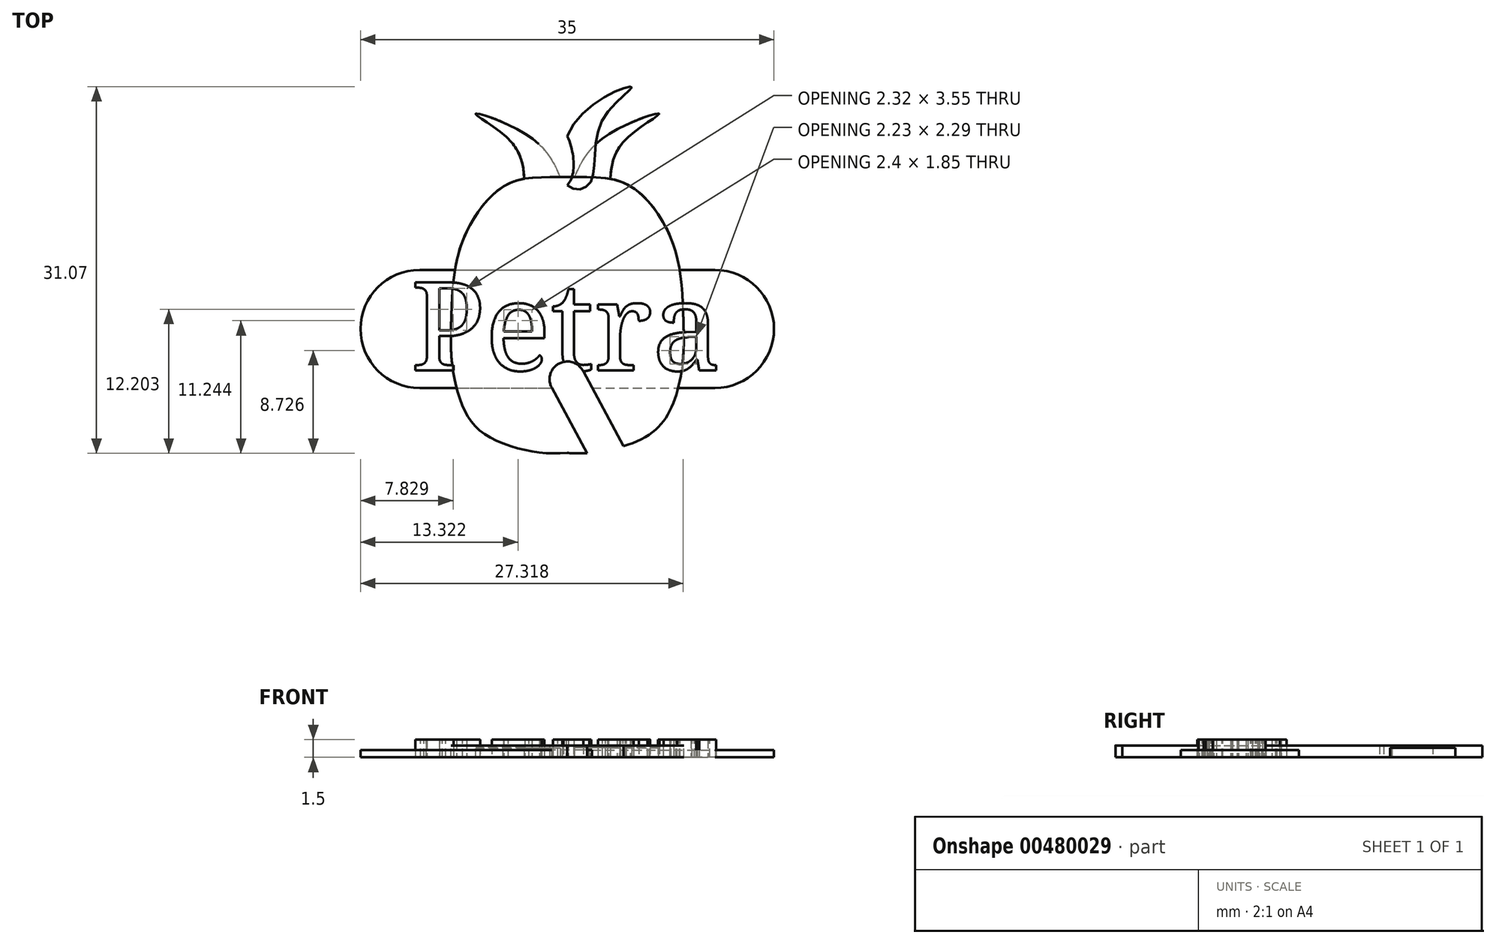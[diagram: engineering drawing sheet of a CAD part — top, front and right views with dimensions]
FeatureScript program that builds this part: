
annotation { "Feature Type Name" : "Feature", "Feature Type Description" : "" }
export const myFeature = defineFeature(function(context is Context, id is Id, definition is map)
    precondition{}
    {
        {
            var Q0;
            Q0=qCreatedBy(makeId("Top.planeOp"),FACE);
            var sketch = newSketch(context, id + "F0", { "sketchPlane" : qUnion([Q0])});
            skText(sketch, "E0", { "text": "Petra", "fontName": "NotoSerif-Regular.ttf"});
            const initialGuessF0  = {"E0": [-0.01327, -0.0075, 1, 0, 0.0075]};
            skSetInitialGuess(sketch, initialGuessF0);
            skSolve(sketch);
        }
        {
            var Q0;
            Q0 = qSketchRegion(id + "F0", true);
            extrude(context, id + "F1", {"entities" : qUnion([Q0]), "depth" : 1.5 * mm, "offsetDistance" : 25 * mm});
        }
        {
            var Q0;
            Q0=qCreatedBy(makeId("Top.planeOp"),FACE);
            var sketch = newSketch(context, id + "F2", { "sketchPlane" : qUnion([Q0])});
            skFitSpline(sketch, "E1", {"points": [v(0, -14.5) * mm, v(-3.65, -14.24) * mm, v(-7.11, -12.83) * mm, v(-8.78, -10.71) * mm, v(-9.74, -7.05) * mm, v(-9.8, -2.69) * mm, v(-9.49, 1.16) * mm, v(-8.52, 4.24) * mm, v(-6.73, 6.94) * mm, v(-4.16, 8.6) * mm, v(0, 8.86) * mm], "startDerivative": vector(-36.01, -3.1) * mm, "endDerivative": vector(39.07, 0.66) * mm});
            skFitSpline(sketch, "E2.MirrorCS", {"points": [v(0, -14.5) * mm, v(3.65, -14.24) * mm, v(7.11, -12.83) * mm, v(8.78, -10.71) * mm, v(9.74, -7.05) * mm, v(9.8, -2.69) * mm, v(9.49, 1.16) * mm, v(8.52, 4.24) * mm, v(6.73, 6.94) * mm, v(4.16, 8.6) * mm, v(0, 8.86) * mm], "startDerivative": vector(36.01, -3.1) * mm, "endDerivative": vector(-39.07, 0.66) * mm});
            skSolve(sketch);
        }
        {
            var Q0;
            Q0=makeQuery(id+"F2.imprint","IMPRINT",FACE,{"disambiguationData":[TD([[makeQuery(id+"F2.imprint","IMPRINT",EDGE,{"derivedFrom":sQuery(id+"F2.wireOp",EDGE,"E1")}),-1.0]])]});
            extrude(context, id + "F3", {"entities" : qUnion([Q0]), "depth" : 1 * mm, "offsetDistance" : 25 * mm});
        }
        {
            var Q0;
            Q0=qCreatedBy(makeId("Top.planeOp"),FACE);
            var sketch = newSketch(context, id + "F4", { "sketchPlane" : qUnion([Q0])});
            skFitSpline(sketch, "E3", {"points": [v(-3.62, 8.13) * mm, v(-4.76, 11.85) * mm, v(-7.76, 14.23) * mm, v(-3.16, 12.26) * mm, v(-0.47, 8.54) * mm], "startDerivative": vector(-0.55, 16.12) * mm, "endDerivative": vector(6.29, -15.12) * mm});
            skLineSegment(sketch, "E4", {"start": v(-3.62, 8.13) * mm, "end": v(-0.47, 8.54) * mm});
            skFitSpline(sketch, "E5.MirrorCS", {"points": [v(3.62, 8.13) * mm, v(4.76, 11.85) * mm, v(7.76, 14.23) * mm, v(3.16, 12.26) * mm, v(0.47, 8.54) * mm], "startDerivative": vector(0.55, 16.12) * mm, "endDerivative": vector(-6.29, -15.12) * mm});
            skLineSegment(sketch, "E6", {"start": v(0.47, 8.54) * mm, "end": v(3.62, 8.13) * mm});
            skSolve(sketch);
        }
        {
            var Q0;
            Q0=makeQuery(id+"F4.imprint","IMPRINT",FACE,{"disambiguationData":[TD([[makeQuery(id+"F4.imprint","IMPRINT",EDGE,{"derivedFrom":sQuery(id+"F4.wireOp",EDGE,"E3")}),-1.0]])]});
            var Q1;
            Q1=makeQuery(id+"F4.imprint","IMPRINT",FACE,{"disambiguationData":[TD([[makeQuery(id+"F4.imprint","IMPRINT",EDGE,{"derivedFrom":sQuery(id+"F4.wireOp",EDGE,"E5.MirrorCS")}),1.0]])]});
            extrude(context, id + "F5", {"entities" : qUnion([Q0, Q1]), "operationType" : NewBodyOperationType.ADD, "depth" : 0.8 * mm, "offsetDistance" : 25 * mm});
        }
        {
            var Q0;
            Q0=qCreatedBy(makeId("Top.planeOp"),FACE);
            var sketch = newSketch(context, id + "F6", { "sketchPlane" : qUnion([Q0])});
            skFitSpline(sketch, "E7", {"points": [v(-1.9, 8.32) * mm, v(-2.9, 13.55) * mm, v(-5.45, 16.5) * mm, v(-0.96, 13.88) * mm, v(0, 8.18) * mm, v(-1.9, 8.32) * mm]});
            skFitSpline(sketch, "E8.MirrorC", {"points": [v(1.9, 8.32) * mm, v(2.9, 13.55) * mm, v(5.45, 16.5) * mm, v(0.96, 13.88) * mm, v(0, 8.18) * mm, v(1.9, 8.32) * mm]});
            skSolve(sketch);
        }
        {
            var Q0;
            {var subQ0=sQuery(id+"F6.wireOp",EDGE,"E8.MirrorC");var subQ1=sQuery(id+"F6.wireOp",EDGE,"E7");var subQ2=makeQuery(id+"F6.imprint","INTERSECT",VERTEX,{"disambiguationData":[OD(0.0)],"derivedFrom":[subQ1,subQ0]});Q0=makeQuery(id+"F6.imprint","IMPRINT",FACE,{"disambiguationData":[TD([[makeQuery(id+"F6.imprint","IMPRINT",EDGE,{"disambiguationData":[TD([[subQ2,-1.0]])],"derivedFrom":subQ1}),-1.0]])]});}
            var Q1;
            {var subQ0=sQuery(id+"F6.wireOp",EDGE,"E8.MirrorC");var subQ1=sQuery(id+"F6.wireOp",EDGE,"E7");var subQ2=makeQuery(id+"F6.imprint","INTERSECT",VERTEX,{"disambiguationData":[OD(0.0)],"derivedFrom":[subQ1,subQ0]});Q1=makeQuery(id+"F6.imprint","IMPRINT",FACE,{"disambiguationData":[TD([[makeQuery(id+"F6.imprint","IMPRINT",EDGE,{"disambiguationData":[TD([[subQ2,1.0]])],"derivedFrom":subQ1}),1.0]])]});}
            extrude(context, id + "F7", {"entities" : qUnion([Q0, Q1]), "depth" : 1 * mm, "offsetDistance" : 25 * mm});
        }
        {
            var Q0;
            Q0=qCreatedBy(makeId("Top.planeOp"),FACE);
            var sketch = newSketch(context, id + "F8", { "sketchPlane" : qUnion([Q0])});
            skLineSegment(sketch, "E9.bottom", {"start": v(-12.5, 1) * mm, "end": v(12.5, 1) * mm});
            skLineSegment(sketch, "E9.top", {"start": v(-12.5, -9) * mm, "end": v(12.5, -9) * mm});
            skArc(sketch, "E10", {"start": v(-12.5, -9) * mm, "mid": v(-17.5, -4) * mm, "end": v(-12.5, 1) * mm});
            skArc(sketch, "E11", {"start": v(12.5, -9) * mm, "mid": v(17.5, -4) * mm, "end": v(12.5, 1) * mm});
            skSolve(sketch);
        }
        {
            var Q0;
            Q0=makeQuery(id+"F8.imprint","IMPRINT",FACE,{"disambiguationData":[TD([[makeQuery(id+"F8.imprint","IMPRINT",EDGE,{"derivedFrom":sQuery(id+"F8.wireOp",EDGE,"E9.bottom")}),-1.0]])]});
            extrude(context, id + "F9", {"entities" : qUnion([Q0]), "depth" : 0.6 * mm, "offsetDistance" : 25 * mm});
        }
        {
            var Q0;
            Q0=qCreatedBy(makeId("Top.planeOp"),FACE);
            var sketch = newSketch(context, id + "F10", { "sketchPlane" : qUnion([Q0])});
            skLineSegment(sketch, "E12", {"start": v(3.92, -18.7) * mm, "end": v(-1.32, -8.97) * mm});
            skLineSegment(sketch, "E13", {"start": v(-1.32, -8.97) * mm, "end": v(1.32, -7.55) * mm, "construction": true});
            skLineSegment(sketch, "E14", {"start": v(1.32, -7.55) * mm, "end": v(6.54, -17.23) * mm});
            skLineSegment(sketch, "E15", {"start": v(6.54, -17.23) * mm, "end": v(3.92, -18.7) * mm});
            skArc(sketch, "E16", {"start": v(-1.32, -8.97) * mm, "mid": v(-0.71, -6.94) * mm, "end": v(1.32, -7.55) * mm});
            skSolve(sketch);
        }
        {
            var Q0;
            Q0=makeQuery(id+"F10.imprint","IMPRINT",FACE,{"disambiguationData":[TD([[makeQuery(id+"F10.imprint","IMPRINT",EDGE,{"derivedFrom":sQuery(id+"F10.wireOp",EDGE,"E12")}),-1.0]])]});
            extrude(context, id + "F11", {"entities" : qUnion([Q0]), "operationType" : NewBodyOperationType.REMOVE, "depth" : 25 * mm, "offsetDistance" : 25 * mm});
        }
    });
